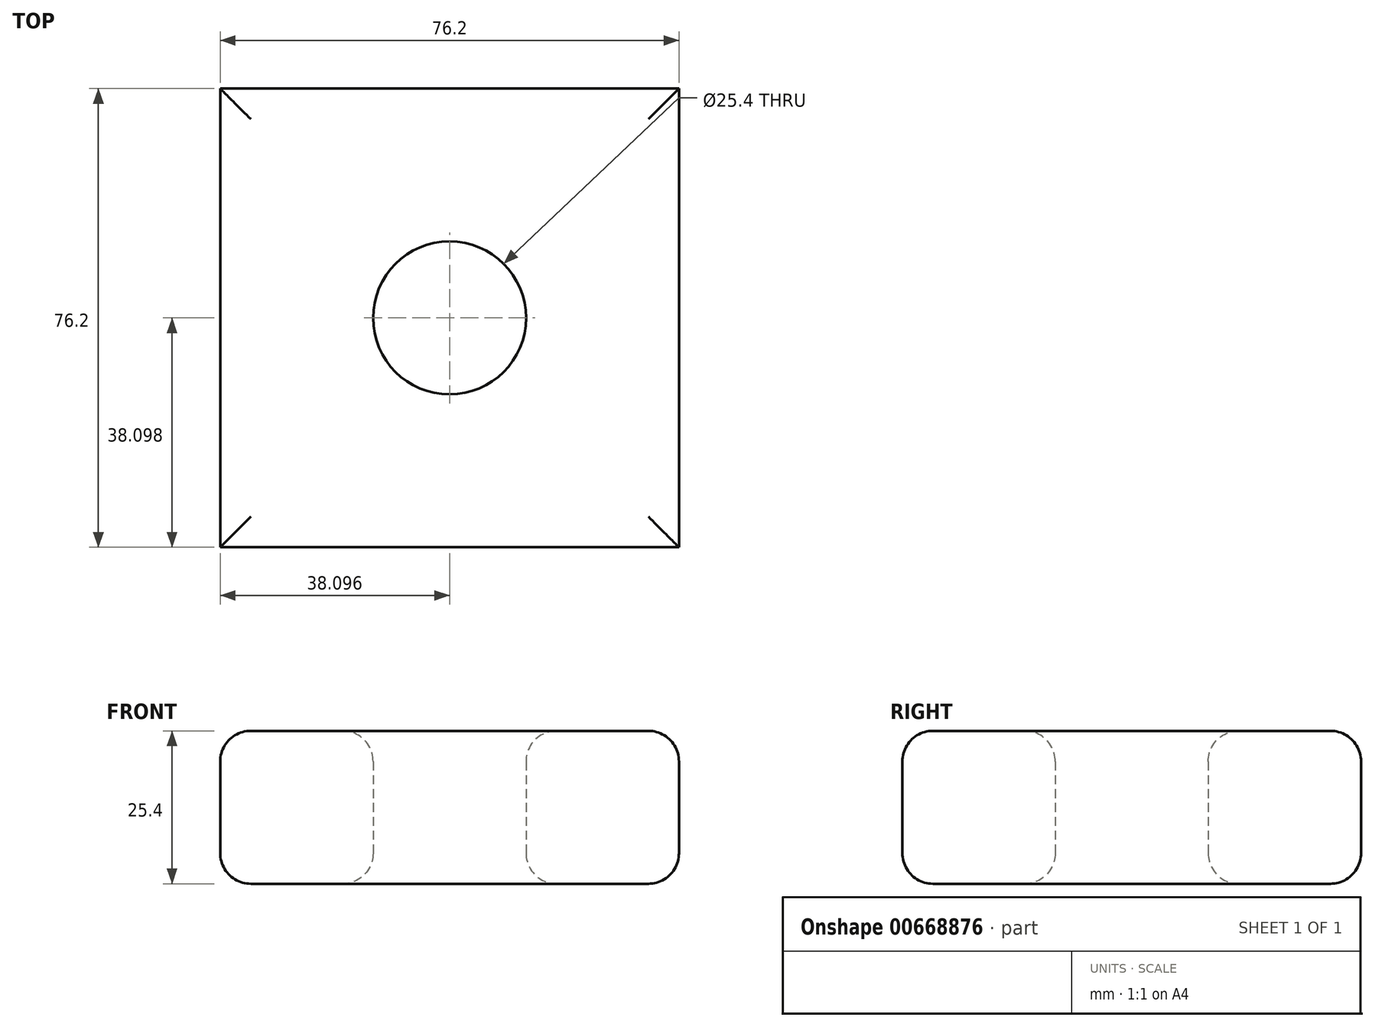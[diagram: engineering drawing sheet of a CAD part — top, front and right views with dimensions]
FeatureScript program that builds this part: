
annotation { "Feature Type Name" : "Feature", "Feature Type Description" : "" }
export const myFeature = defineFeature(function(context is Context, id is Id, definition is map)
    precondition{}
    {
        {
            var Q0;
            Q0=qCreatedBy(makeId("Top.planeOp"),FACE);
            var sketch = newSketch(context, id + "F0", { "sketchPlane" : qUnion([Q0])});
            skLineSegment(sketch, "E0.bottom", {"start": v(32.68, -42.95) * mm, "end": v(-43.52, -42.95) * mm});
            skLineSegment(sketch, "E0.top", {"start": v(32.68, 33.25) * mm, "end": v(-43.52, 33.25) * mm});
            skLineSegment(sketch, "E0.left", {"start": v(32.68, -42.95) * mm, "end": v(32.68, 33.25) * mm});
            skLineSegment(sketch, "E0.right", {"start": v(-43.52, -42.95) * mm, "end": v(-43.52, 33.25) * mm});
            skCircle(sketch, "E1", {"center": v(-5.42, -4.85) * mm, "radius": 12.7 * mm});
            skSolve(sketch);
        }
        {
            var Q0;
            Q0 = qSketchRegion(id + "F0", true);
            extrude(context, id + "F1", {"entities" : qUnion([Q0]), "depth" : 25.4 * mm, "offsetDistance" : 25.4 * mm});
        }
        {
            var Q0;
            Q0=makeQuery(id+"F1.opExtrude","CAP_FACE",FACE,{"disambiguationData":[OSD([sQuery(id+"F0.wireOp",EDGE,"E0.bottom"),sQuery(id+"F0.wireOp",EDGE,"E0.top"),sQuery(id+"F0.wireOp",EDGE,"E0.left"),sQuery(id+"F0.wireOp",EDGE,"E0.right"),sQuery(id+"F0.wireOp",EDGE,"E1")])],"isStart":false});
            var Q1;
            Q1=makeQuery(id+"F1.opExtrude","CAP_FACE",FACE,{"disambiguationData":[OSD([sQuery(id+"F0.wireOp",EDGE,"E0.bottom"),sQuery(id+"F0.wireOp",EDGE,"E0.top"),sQuery(id+"F0.wireOp",EDGE,"E0.left"),sQuery(id+"F0.wireOp",EDGE,"E0.right"),sQuery(id+"F0.wireOp",EDGE,"E1")])],"isStart":true});
            fillet(context, id + "F2", {"entities" : qUnion([Q0, Q1]), "radius" : 5.08 * mm, "tangentPropagation" : true, "allowEdgeOverflow" : false});
        }
    });
